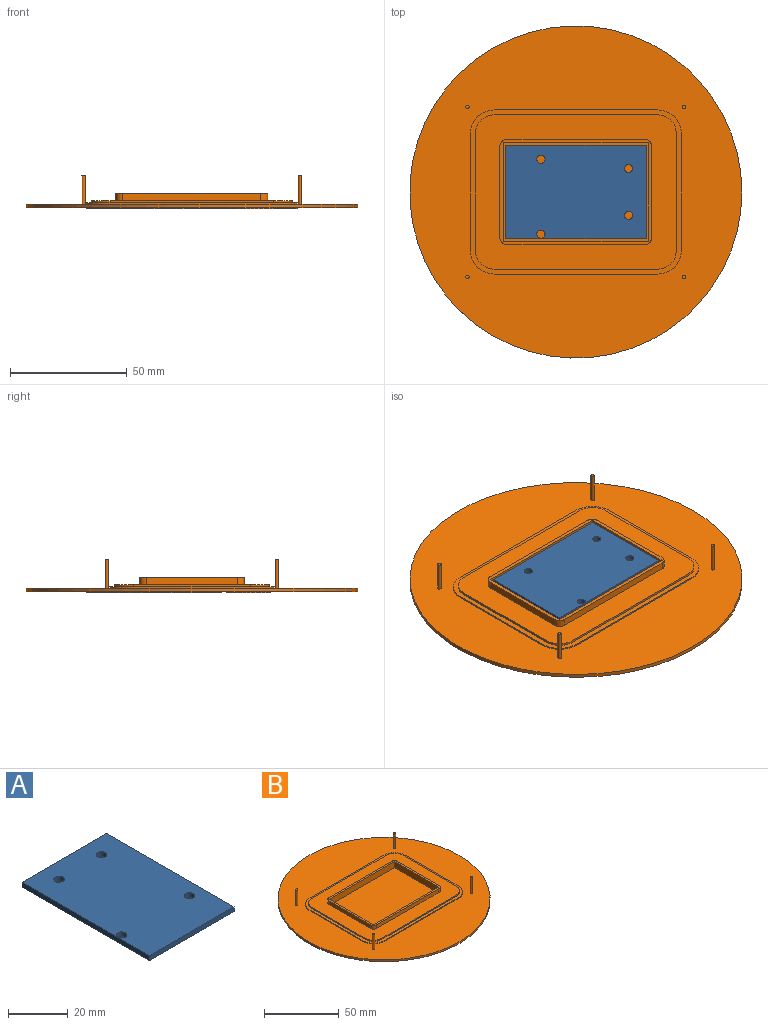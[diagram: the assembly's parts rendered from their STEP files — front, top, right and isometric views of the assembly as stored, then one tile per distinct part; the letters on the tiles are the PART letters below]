
ASSEMBLY  parts=2 mates=1
PART A: 10 faces, bbox 40x60x2 mm
  f0: plane 40x2mm, normal (0,1,0), area 80mm2, adj f1,f3,f4,f5
  f1: plane 60x2mm, normal (-1,0,0), area 120mm2, adj f0,f2,f4,f5
  f2: plane 40x2mm, normal (0,-1,0), area 80mm2, adj f1,f3,f4,f5
  f3: plane 60x2mm, normal (1,0,0), area 120mm2, adj f0,f2,f4,f5
  f4: plane 60x40mm, normal (0,0,1), area 2361.5mm2, adj f0,f1,f2,f3,f6,f7,f8,f9
  f5: plane 60x40mm, normal (0,0,-1), area 2361.5mm2, adj f0,f1,f2,f3,f6,f7,f8,f9
  f6: cylinder r=1.75mm len=3.5mm, axis (0,0,-1), area 22mm2, adj f4,f5
  f7: cylinder r=1.75mm len=3.5mm, axis (0,0,-1), area 22mm2, adj f4,f5
  f8: cylinder r=1.75mm len=3.5mm, axis (0,0,-1), area 22mm2, adj f4,f5
  f9: cylinder r=1.75mm len=3.5mm, axis (0,0,-1), area 22mm2, adj f4,f5
PART B: 50 faces, bbox 142.1x142.1x14.5 mm
  f0: plane 86x66mm, normal (0,0,1), area 2703.8mm2, adj f13,f14,f15,f16,f17,f18,f19,f20
  f1: plane 142.13x142.13mm, normal (0,0,-1), area 12162.3mm2, adj f2,f30,f32,f34
  f2: cylinder r=71.06mm len=142.13mm, axis (0,0,-1), area 669.8mm2, adj f1,f3
  f3: plane 142.13x142.13mm, normal (0,0,1), area 9613.5mm2, adj f2,f4,f5,f6,f7,f8,f9,f10
  f4: plane 50x0.6mm, normal (-1,0,0), area 30mm2, adj f3,f5,f11,f12
  f5: cylinder r=10.1mm len=10.1mm, axis (0,0,-1), area 9.5mm2, adj f3,f4,f6,f12
  f6: plane 70x0.6mm, normal (0,-1,0), area 42mm2, adj f3,f5,f7,f12
  f7: cylinder r=10.1mm len=10.1mm, axis (0,0,-1), area 9.5mm2, adj f3,f6,f8,f12
  f8: plane 50x0.6mm, normal (1,0,0), area 30mm2, adj f3,f7,f9,f12
  f9: cylinder r=10.1mm len=10.1mm, axis (0,0,-1), area 9.5mm2, adj f3,f8,f10,f12
  f10: plane 70x0.6mm, normal (0,1,0), area 42mm2, adj f3,f9,f11,f12
  f11: cylinder r=10.1mm len=10.1mm, axis (0,0,-1), area 9.5mm2, adj f3,f4,f10,f12
  f12: plane 90.2x70.2mm, normal (0,0,1), area 623.4mm2, adj f4,f5,f6,f7,f8,f9,f10,f11
  f13: cylinder r=8mm len=8mm, axis (0,0,-1), area 11.3mm2, adj f0,f12,f14,f20
  f14: plane 70x0.9mm, normal (0,1,0), area 63mm2, adj f0,f12,f13,f15
  f15: cylinder r=8mm len=8mm, axis (0,0,-1), area 11.3mm2, adj f0,f12,f14,f16
  f16: plane 50x0.9mm, normal (1,0,0), area 45mm2, adj f0,f12,f15,f17
  f17: cylinder r=8mm len=8mm, axis (0,0,-1), area 11.3mm2, adj f0,f12,f16,f18
  f18: plane 70x0.9mm, normal (0,-1,0), area 63mm2, adj f0,f12,f17,f19
  f19: cylinder r=8mm len=8mm, axis (0,0,-1), area 11.3mm2, adj f0,f12,f18,f20
  f20: plane 50x0.9mm, normal (-1,0,0), area 45mm2, adj f0,f12,f13,f19
  f21: cylinder r=0.75mm len=12.5mm, axis (0,0,-1), area 58.9mm2, adj f3,f22
  f22: plane 1.5x1.5mm, normal (0,0,1), area 1.8mm2, adj f21
  f23: cylinder r=0.75mm len=12.5mm, axis (0,0,-1), area 58.9mm2, adj f3,f24
  f24: plane 1.5x1.5mm, normal (0,0,1), area 1.8mm2, adj f23
  f25: cylinder r=0.75mm len=12.5mm, axis (0,0,-1), area 58.9mm2, adj f3,f26
  f26: plane 1.5x1.5mm, normal (0,0,1), area 1.8mm2, adj f25
  f27: cylinder r=0.75mm len=12.5mm, axis (0,0,-1), area 58.9mm2, adj f3,f28
  f28: plane 1.5x1.5mm, normal (0,0,1), area 1.8mm2, adj f27
  f29: extruded ~90x21.66mm, area 25.7mm2, adj f30,f31,f33
  f30: cylinder r=45mm len=90mm, axis (0,0,1), area 70.7mm2, adj f1,f29,f31,f32
  f31: plane 90x48.76mm, normal (0,0,-1), area 2419.6mm2, adj f29,f30
  f32: extruded ~90x15.51mm, area 24.5mm2, adj f1,f30,f33
  f33: plane 90x34.58mm, normal (0,0,-1), area 1009.7mm2, adj f29,f32
  f34: cylinder r=9.33mm len=18.66mm, axis (0,0,1), area 29.3mm2, adj f1,f35
  f35: plane 18.66x18.66mm, normal (0,0,-1), area 273.5mm2, adj f34
  f36: plane 59x3mm, normal (0,1,0), area 177mm2, adj f0,f40,f46,f49
  f37: plane 39x3mm, normal (-1,0,0), area 117mm2, adj f0,f40,f46,f47
  f38: plane 59x3mm, normal (0,-1,0), area 177mm2, adj f0,f40,f47,f48
  f39: plane 39x3mm, normal (1,0,0), area 117mm2, adj f0,f40,f48,f49
  f40: plane 65x45mm, normal (0,0,1), area 313.3mm2, adj f36,f37,f38,f39,f42,f43,f44,f45
  f41: plane 62x42mm, normal (0,0,1), area 2604mm2, adj f42,f43,f44,f45
  f42: plane 62x5mm, normal (0,1,0), area 310mm2, adj f40,f41,f43,f45
  f43: plane 42x5mm, normal (-1,0,0), area 210mm2, adj f40,f41,f42,f44
  f44: plane 62x5mm, normal (0,-1,0), area 310mm2, adj f40,f41,f43,f45
  f45: plane 42x5mm, normal (1,0,0), area 210mm2, adj f40,f41,f42,f44
  f46: cylinder r=3mm len=3mm, axis (0,0,1), area 14.1mm2, adj f0,f36,f37,f40
  f47: cylinder r=3mm len=3mm, axis (0,0,-1), area 14.1mm2, adj f0,f37,f38,f40
  f48: cylinder r=3mm len=3mm, axis (0,0,1), area 14.1mm2, adj f0,f38,f39,f40
  f49: cylinder r=3mm len=3mm, axis (0,0,-1), area 14.1mm2, adj f0,f36,f39,f40
PLACE A rot(axis=(0.71,0.71,0),180deg) t=(-6.58,-1.92,2.04)mm
PLACE B t=(-6.64,-1.91,-3.86)mm
MATE parallel A.f4 <-> B.f2  axis (0,0,-1) through (-6.64,-1.91,0.04)mm
